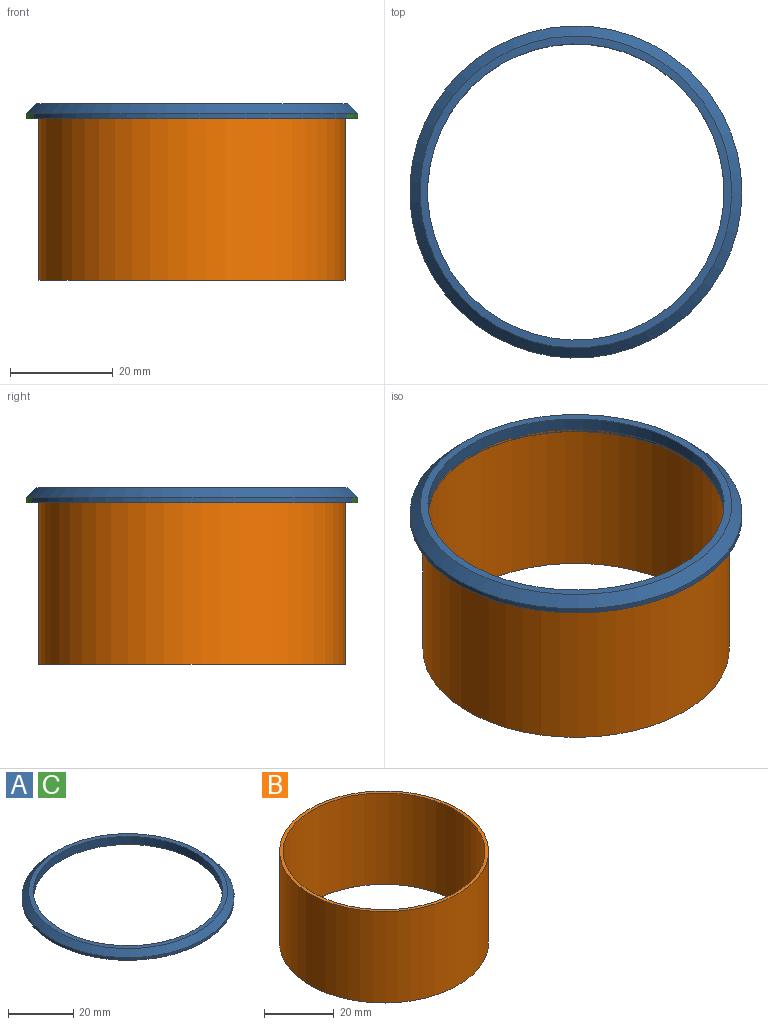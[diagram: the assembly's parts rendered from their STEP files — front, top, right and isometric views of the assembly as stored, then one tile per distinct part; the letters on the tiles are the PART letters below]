
ASSEMBLY  parts=3 mates=1
PART A: 5 faces, bbox 64.8x64.8x3 mm
  f0: cylinder r=28.9mm len=57.8mm, axis (0,0,-1), area 544.8mm2, adj f2,f3
  f1: cylinder r=32.4mm len=64.8mm, axis (0,0,-1), area 203.6mm2, adj f3,f4
  f2: plane 60.8x60.8mm, normal (0,0,1), area 279.4mm2, adj f0,f4
  f3: plane 64.8x64.8mm, normal (0,0,-1), area 674mm2, adj f0,f1
  f4: cone r=30.4mm half-angle=45deg, axis (0,0,-1), area 558mm2, adj f1,f2
PART B: 4 faces, bbox 59.8x59.8x32 mm
  f0: cylinder r=29.9mm len=59.8mm, axis (0,0,-1), area 6011.8mm2, adj f1,f2
  f1: plane 59.8x59.8mm, normal (0,0,1), area 184.7mm2, adj f0,f3
  f2: plane 59.8x59.8mm, normal (0,0,-1), area 184.7mm2, adj f0,f3
  f3: cylinder r=28.9mm len=57.8mm, axis (0,0,1), area 5810.7mm2, adj f1,f2
PART C: same geometry as A
PLACE A at identity
PLACE B t=(0,0,-31.5)mm
PLACE C at identity
MATE fastened B.f0 <-> A.f1  axis (0,0,1) through (0,0,0.5)mm
